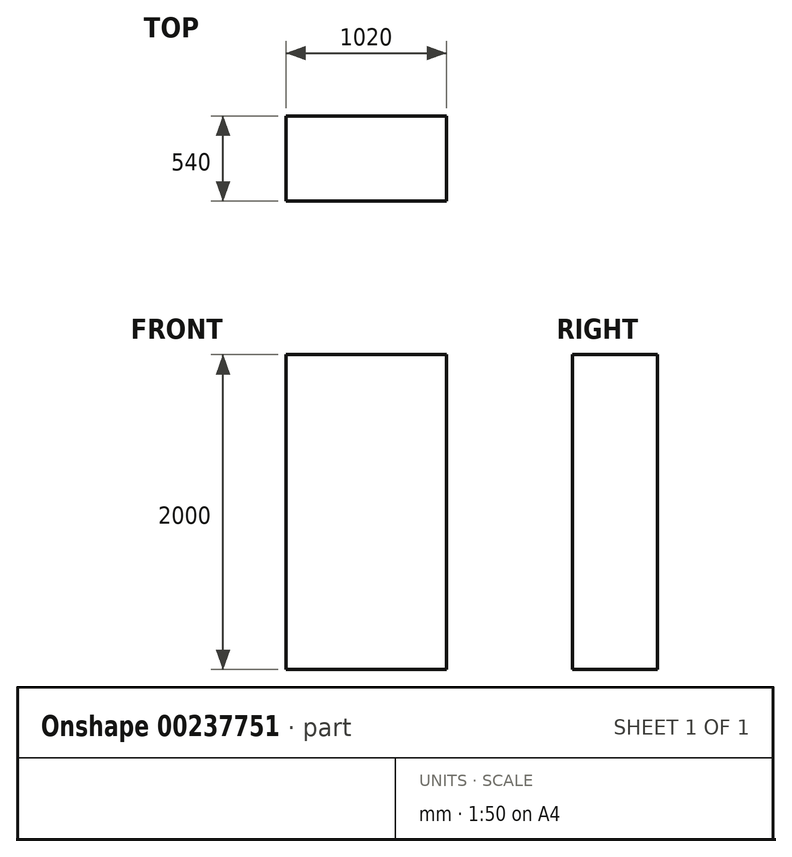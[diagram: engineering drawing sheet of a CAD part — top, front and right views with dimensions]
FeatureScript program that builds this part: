
annotation { "Feature Type Name" : "Feature", "Feature Type Description" : "" }
export const myFeature = defineFeature(function(context is Context, id is Id, definition is map)
    precondition{}
    {
        {
            var Q0;
            Q0=qCreatedBy(makeId("Top.planeOp"),FACE);
            var sketch = newSketch(context, id + "F0", { "sketchPlane" : qUnion([Q0])});
            skLineSegment(sketch, "E0.bottom", {"start": v(0, 0) * mm, "end": v(-1020, 0) * mm});
            skLineSegment(sketch, "E0.top", {"start": v(0, 540) * mm, "end": v(-1020, 540) * mm});
            skLineSegment(sketch, "E0.left", {"start": v(0, 0) * mm, "end": v(0, 540) * mm});
            skLineSegment(sketch, "E0.right", {"start": v(-1020, 0) * mm, "end": v(-1020, 540) * mm});
            skSolve(sketch);
        }
        {
            var Q0;
            Q0=makeQuery(id+"F0.imprint","IMPRINT",FACE,{"disambiguationData":[TD([[makeQuery(id+"F0.imprint","IMPRINT",EDGE,{"derivedFrom":sQuery(id+"F0.wireOp",EDGE,"E0.bottom")}),-1.0]])]});
            extrude(context, id + "F1", {"entities" : qUnion([Q0]), "depth" : 2000 * mm});
        }
    });
